# Revit family: Midea_VRF_Outdoor_Vi_MDVT-V280(335)WDGN1(50_60Hz)
name_source: partatom
category: Mechanical Equipment
revit_build: Autodesk Revit 2013 (Build: 20120221_2030(x64)
units: mm (PartAtom-declared; Revit-internal decimal feet)

## types (2) — shared parameters
Casing color = SB2014
Compressor = 1
Condensation = air
Depth = 528 mm  [stored 1.73228 ft]
Description = High efficiency air cooled
Gas = R410a
Gas pipe = 25.4 mm  [stored 0.0833333 ft]
Gas pipe Radius = 12.7 mm  [stored 0.0416667 ft]
Height = 1558 mm  [stored 5.11155 ft]
Installation = outdoor installation
MCA (Minimum Circuit Amps) = 26 A
MFA (Maximum Fuse Amps) = 32 A
Machine material = Galvanized Steel
Manufacturer = Midea
Net Weight = 157.00 kg
Power supply = 380-415V 3N~50Hz/60Hz
Series = VRF
Width = 1120 mm  [stored 3.67454 ft]
clearance access behind = 300 mm
clearance access front = 300 mm
clearance access left = 600 mm
clearance access right = 300 mm

## per-type parameters (varying)
| type | Air Flow | Cooling Capacity | Cooling Power Input | Heating Capacity | Heating Power Input | Liquid pipe | Liquid pipe Radius |
| MDVT-V280W/DGN1 | 11000.000 m³/h | 28 kW | 7 kW | 32 kW | 8 kW | 9.53 mm | 4.765 mm |
| MDVT-V335W/DGN1 | 11300.000 m³/h | 34 kW | 9 kW | 38 kW | 9 kW | 12.7 mm  [stored 0.0416667 ft] | 6.35 mm  [stored 0.0208333 ft] |

note: column(s) folded — value = type name in every type: Model

note: [stored X ft] marks values corroborated as IEEE doubles in the binary element streams (Revit-internal decimal feet)

## geometry (parser evidence)
native form markers: Sweep x3
no freeform markers — native parametric forms only
